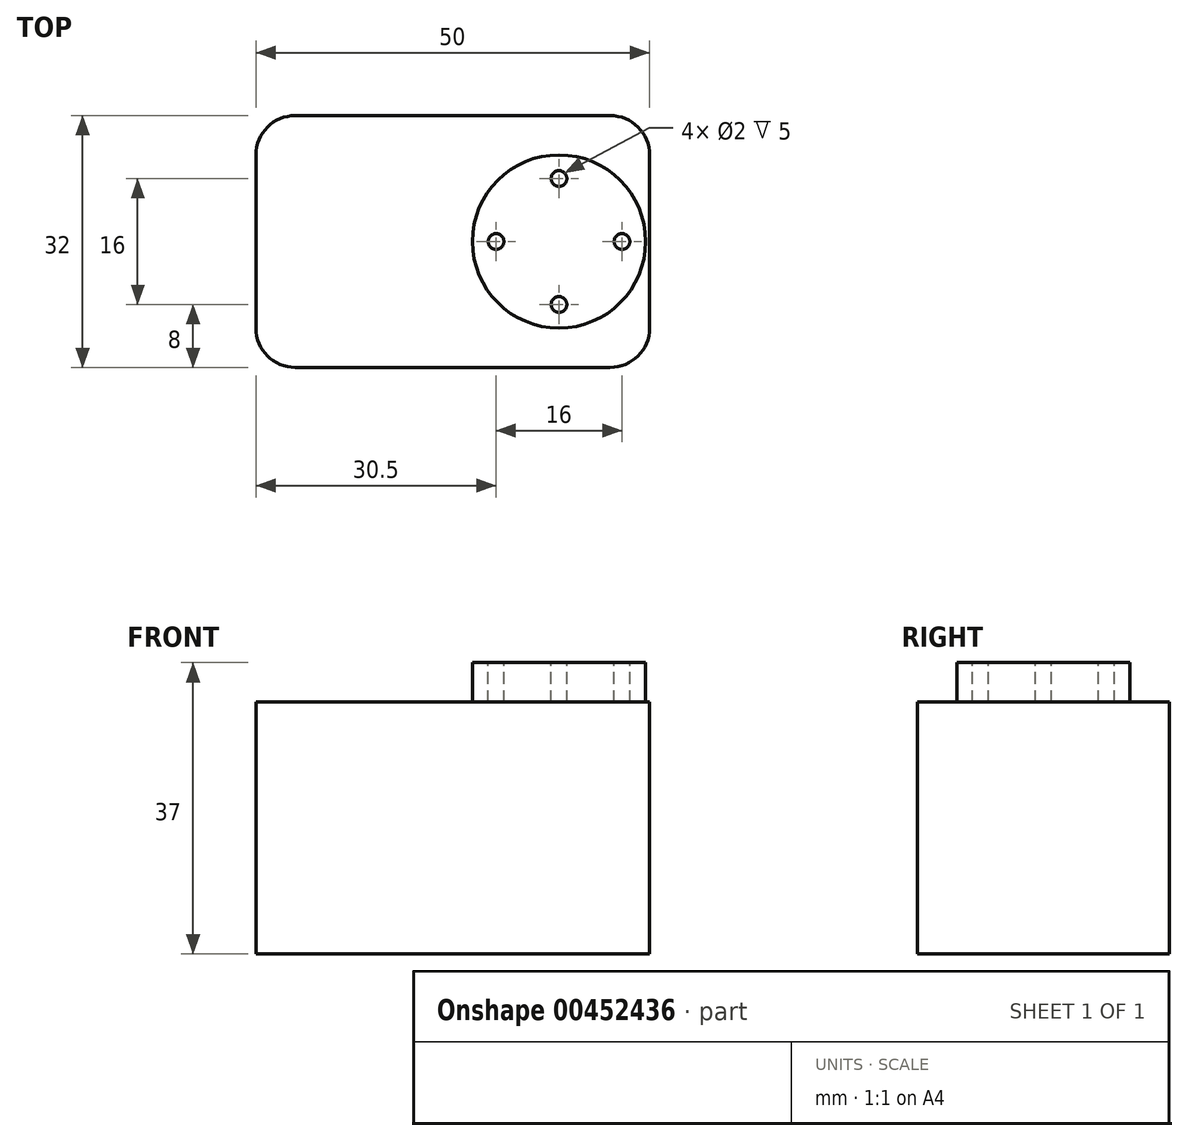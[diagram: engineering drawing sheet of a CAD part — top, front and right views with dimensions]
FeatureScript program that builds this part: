
annotation { "Feature Type Name" : "Feature", "Feature Type Description" : "" }
export const myFeature = defineFeature(function(context is Context, id is Id, definition is map)
    precondition{}
    {
        {
            var Q0;
            Q0=qCreatedBy(makeId("Top.planeOp"),FACE);
            var sketch = newSketch(context, id + "F0", { "sketchPlane" : qUnion([Q0])});
            skLineSegment(sketch, "E0.bottom", {"start": v(25, -16) * mm, "end": v(-25, -16) * mm});
            skLineSegment(sketch, "E0.top", {"start": v(25, 16) * mm, "end": v(-25, 16) * mm});
            skLineSegment(sketch, "E0.left", {"start": v(25, -16) * mm, "end": v(25, 16) * mm});
            skLineSegment(sketch, "E0.right", {"start": v(-25, -16) * mm, "end": v(-25, 16) * mm});
            skPoint(sketch, "E0.middle", {"position": v(0, 0) * mm});
            skSolve(sketch);
        }
        {
            var Q0;
            Q0=makeQuery(id+"F0.imprint","IMPRINT",FACE,{"disambiguationData":[TD([[makeQuery(id+"F0.imprint","IMPRINT",EDGE,{"derivedFrom":sQuery(id+"F0.wireOp",EDGE,"E0.bottom")}),-1.0]])]});
            extrude(context, id + "F1", {"entities" : qUnion([Q0]), "depth" : 32 * mm});
        }
        {
            var Q0;
            Q0=makeQuery(id+"F1.opExtrude","SWEPT_EDGE",EDGE,{"disambiguationData":[OSD([sQuery(id+"F0.wireOp",EDGE,"E0.bottom"),sQuery(id+"F0.wireOp",EDGE,"E0.right")])]});
            var Q1;
            Q1=makeQuery(id+"F1.opExtrude","SWEPT_EDGE",EDGE,{"disambiguationData":[OSD([sQuery(id+"F0.wireOp",EDGE,"E0.top"),sQuery(id+"F0.wireOp",EDGE,"E0.right")])]});
            var Q2;
            Q2=makeQuery(id+"F1.opExtrude","SWEPT_EDGE",EDGE,{"disambiguationData":[OSD([sQuery(id+"F0.wireOp",EDGE,"E0.bottom"),sQuery(id+"F0.wireOp",EDGE,"E0.left")])]});
            var Q3;
            Q3=makeQuery(id+"F1.opExtrude","SWEPT_EDGE",EDGE,{"disambiguationData":[OSD([sQuery(id+"F0.wireOp",EDGE,"E0.top"),sQuery(id+"F0.wireOp",EDGE,"E0.left")])]});
            fillet(context, id + "F2", {"entities" : qUnion([Q0, Q1, Q2, Q3]), "radius" : 5 * mm, "tangentPropagation" : true, "allowEdgeOverflow" : false});
        }
        {
            var Q0;
            Q0=makeQuery(id+"F1.opExtrude","CAP_FACE",FACE,{"disambiguationData":[OSD([sQuery(id+"F0.wireOp",EDGE,"E0.bottom"),sQuery(id+"F0.wireOp",EDGE,"E0.top"),sQuery(id+"F0.wireOp",EDGE,"E0.left"),sQuery(id+"F0.wireOp",EDGE,"E0.right")])],"isStart":false});
            var sketch = newSketch(context, id + "F3", { "sketchPlane" : qUnion([Q0])});
            skLineSegment(sketch, "E1", {"start": v(25, 0) * mm, "end": v(13.5, 0) * mm, "construction": true});
            skPoint(sketch, "E1.endSnap0", {"position": v(25, 0) * mm});
            skCircle(sketch, "E2", {"center": v(13.5, 0) * mm, "radius": 11 * mm});
            skSolve(sketch);
        }
        {
            var Q0;
            Q0=makeQuery(id+"F3.imprint","IMPRINT",FACE,{"disambiguationData":[TD([[makeQuery(id+"F3.imprint","IMPRINT",EDGE,{"derivedFrom":sQuery(id+"F3.wireOp",EDGE,"E2")}),1.0]])]});
            extrude(context, id + "F4", {"entities" : qUnion([Q0]), "operationType" : NewBodyOperationType.ADD, "depth" : 5 * mm});
        }
        {
            var Q0;
            Q0=makeQuery(id+"F4.opExtrude","CAP_FACE",FACE,{"disambiguationData":[OSD([sQuery(id+"F3.wireOp",EDGE,"E2")])],"isStart":false});
            var sketch = newSketch(context, id + "F5", { "sketchPlane" : qUnion([Q0])});
            skCircle(sketch, "E3", {"center": v(13.5, 0) * mm, "radius": 8 * mm, "construction": true});
            skCircle(sketch, "E4", {"center": v(21.5, 0) * mm, "radius": 1 * mm});
            skCircle(sketch, "E5", {"center": v(13.5, 8) * mm, "radius": 1 * mm});
            skCircle(sketch, "E6", {"center": v(5.5, 0) * mm, "radius": 1 * mm});
            skCircle(sketch, "E7", {"center": v(13.5, -8) * mm, "radius": 1 * mm});
            skSolve(sketch);
        }
        {
            var Q0;
            Q0 = qSketchRegion(id + "F5", true);
            extrude(context, id + "F6", {"entities" : qUnion([Q0]), "operationType" : NewBodyOperationType.REMOVE, "oppositeDirection" : true, "depth" : 5 * mm});
        }
    });
